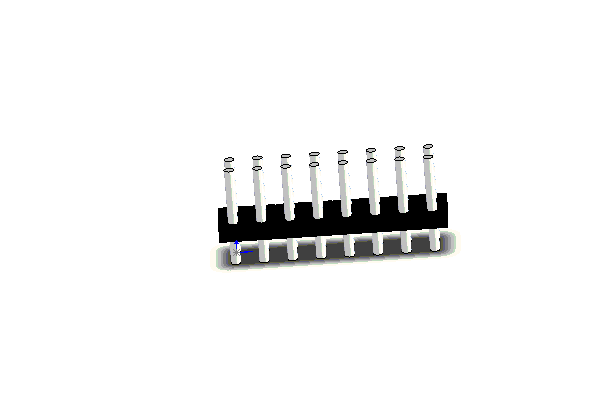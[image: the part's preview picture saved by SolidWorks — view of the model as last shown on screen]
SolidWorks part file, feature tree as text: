
SOLIDWORKS PART (.sldprt)
format: sldprt  version: not decoded by parser v0  size: 179,712 bytes
history: native  units: mm
features: sketch x3, extrude x3, pattern_linear x2, material x1 (+13 scaffold rows collapsed)
feature tree (22):
  scaffold x13  (default folders/planes/origin — collapsed)
  material  "Material <not specified>"
  sketch  "Sketch1"  dims[D1=0.889mm]
  extrude  "Extrude1"  Depth=2.54mm
  sketch  "Sketch2"  dims[D1=1.27mm D2=1.27mm D3=20.32mm D4=5.08mm]
  pattern_linear  "LPattern3"  Count1=8 Count2=2 Spacing1=2.54mm Spacing2=2.54mm
  extrude  "Extrude2"  Depth=1.27mm
  extrude  "Extrude3"  [1 undecoded]
  sketch  "Sketch1<2>"  dims[D1=8.89mm]
  pattern_linear  "LPattern4"  Count1=8 Count2=2 Spacing1=2.54mm Spacing2=2.54mm
decode coverage: 7 of 8 modeling features carry decoded parameters
note: 1 parameter value undecoded
note: suppression state not decoded; provenance and decode notes live in map.json
